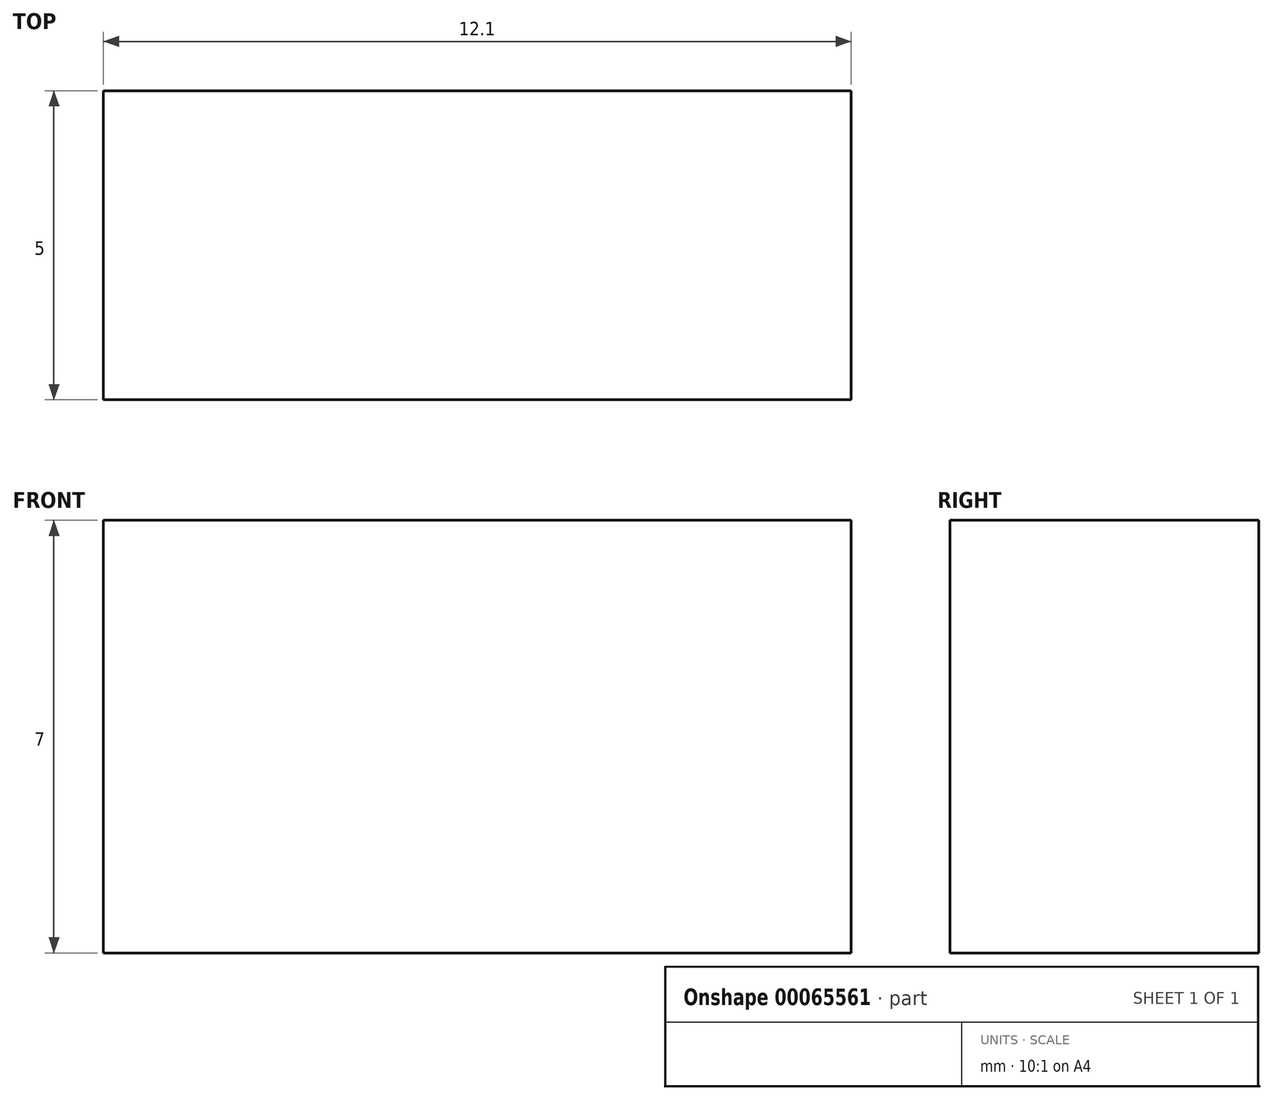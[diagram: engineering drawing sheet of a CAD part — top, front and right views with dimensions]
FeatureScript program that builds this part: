
annotation { "Feature Type Name" : "Feature", "Feature Type Description" : "" }
export const myFeature = defineFeature(function(context is Context, id is Id, definition is map)
    precondition{}
    {
        {
            var Q0;
            Q0=qCreatedBy(makeId("Top.planeOp"),FACE);
            var sketch = newSketch(context, id + "F0", { "sketchPlane" : qUnion([Q0])});
            skLineSegment(sketch, "E0.bottom", {"start": v(6.05, -2.5) * mm, "end": v(-6.05, -2.5) * mm});
            skLineSegment(sketch, "E0.top", {"start": v(6.05, 2.5) * mm, "end": v(-6.05, 2.5) * mm});
            skLineSegment(sketch, "E0.left", {"start": v(6.05, -2.5) * mm, "end": v(6.05, 2.5) * mm});
            skLineSegment(sketch, "E0.right", {"start": v(-6.05, -2.5) * mm, "end": v(-6.05, 2.5) * mm});
            skPoint(sketch, "E0.middle", {"position": v(0, 0) * mm});
            skSolve(sketch);
        }
        {
            var Q0;
            Q0=makeQuery(id+"F0.imprint","IMPRINT",FACE,{"disambiguationData":[TD([[makeQuery(id+"F0.imprint","IMPRINT",EDGE,{"derivedFrom":sQuery(id+"F0.wireOp",EDGE,"E0.bottom")}),-1.0]])]});
            extrude(context, id + "F1", {"entities" : qUnion([Q0]), "depth" : 7 * mm});
        }
        {
            var Q0;
            Q0=makeQuery(id+"F1.opExtrude","SWEPT_BODY",BODY,{"disambiguationData":[OSD([sQuery(id+"F0.wireOp",EDGE,"E0.bottom"),sQuery(id+"F0.wireOp",EDGE,"E0.top"),sQuery(id+"F0.wireOp",EDGE,"E0.left"),sQuery(id+"F0.wireOp",EDGE,"E0.right")])]});
            transform(context, id + "F2", {"entities" : qUnion([Q0]), "transformType" : TransformType.TRANSLATION_3D, "dx" : 0 * mm, "dy" : 0 * mm, "dz" : 0 * mm, "makeCopy" : true});
        }
    });
